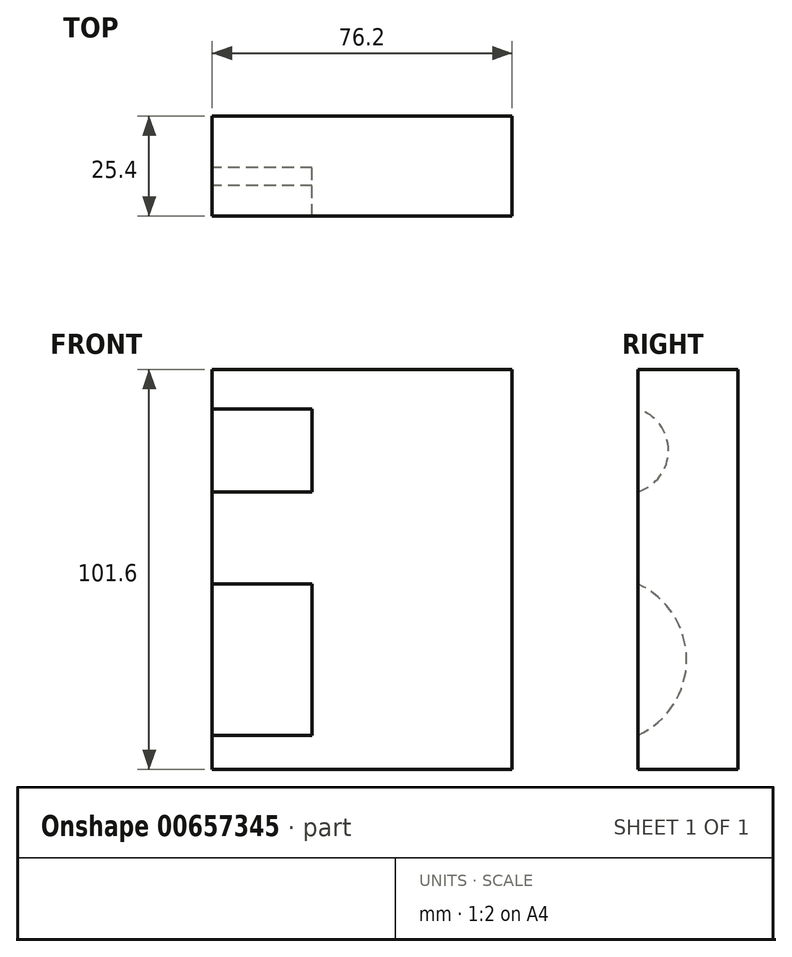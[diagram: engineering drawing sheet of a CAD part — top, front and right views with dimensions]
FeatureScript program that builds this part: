
annotation { "Feature Type Name" : "Feature", "Feature Type Description" : "" }
export const myFeature = defineFeature(function(context is Context, id is Id, definition is map)
    precondition{}
    {
        {
            var Q0;
            Q0=qCreatedBy(makeId("Front.planeOp"),FACE);
            var sketch = newSketch(context, id + "F0", { "sketchPlane" : qUnion([Q0])});
            skLineSegment(sketch, "E0.bottom", {"start": v(0, 0) * mm, "end": v(76.2, 0) * mm});
            skLineSegment(sketch, "E0.top", {"start": v(0, 101.6) * mm, "end": v(76.2, 101.6) * mm});
            skLineSegment(sketch, "E0.left", {"start": v(0, 0) * mm, "end": v(0, 101.6) * mm});
            skLineSegment(sketch, "E0.right", {"start": v(76.2, 0) * mm, "end": v(76.2, 101.6) * mm});
            skSolve(sketch);
        }
        {
            var Q0;
            Q0=makeQuery(id+"F0.imprint","IMPRINT",FACE,{"disambiguationData":[TD([[makeQuery(id+"F0.imprint","IMPRINT",EDGE,{"derivedFrom":sQuery(id+"F0.wireOp",EDGE,"E0.bottom")}),1.0]])]});
            extrude(context, id + "F1", {"entities" : qUnion([Q0]), "depth" : 25.4 * mm, "offsetDistance" : 25.4 * mm});
        }
        {
            var Q0;
            Q0=makeQuery(id+"F1.opExtrude","SWEPT_FACE",FACE,{"disambiguationData":[OSD([sQuery(id+"F0.wireOp",EDGE,"E0.left")])]});
            var sketch = newSketch(context, id + "F2", { "sketchPlane" : qUnion([Q0])});
            skCircle(sketch, "E1", {"center": v(28.72, 81.05) * mm, "radius": 11.04 * mm});
            skCircle(sketch, "E2", {"center": v(34.2, 27.89) * mm, "radius": 21.13 * mm});
            skSolve(sketch);
        }
        {
            var Q0;
            Q0 = qSketchRegion(id + "F2", true);
            extrude(context, id + "F3", {"entities" : qUnion([Q0]), "operationType" : NewBodyOperationType.REMOVE, "oppositeDirection" : true, "depth" : 25.4 * mm, "offsetDistance" : 25.4 * mm});
        }
    });
